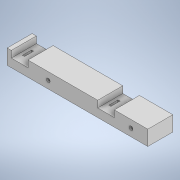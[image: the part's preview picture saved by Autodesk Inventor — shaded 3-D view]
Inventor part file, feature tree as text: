
AUTODESK INVENTOR PART (.ipt)
format: ipt  version: 2020 (Build 240168000, 168)  size: 169,984 bytes
history: native  units: mm
features: extrude x3, sketch x3, projected_geometry x3, other x2
ambient origin geometry x8: Origin, YZ Plane, XZ Plane, XY Plane, X Axis, Y Axis, Z Axis, Center Point
bodies: Body1 (feature_tree)
feature tree (11):
  other  "작업 평면1"
  extrude  "돌출1"  Depth=18.0mm
  extrude  "돌출2"  Depth=8.0mm
  extrude  "돌출3"  Depth=8.0mm
  sketch  "스케치1"
  projected_geometry  "투영된 루프1"
  sketch  "스케치2"
  sketch  "스케치3"
  projected_geometry  "투영된 루프2"
  projected_geometry  "투영된 루프3"
  other  "솔리드1"
